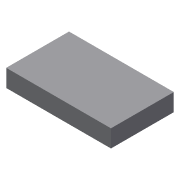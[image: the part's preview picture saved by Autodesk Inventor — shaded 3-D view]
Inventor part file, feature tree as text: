
AUTODESK INVENTOR PART (.ipt)
format: ipt  version: 2019 (Build 230136000, 136)  size: 72,192 bytes
history: native  units: mm
features: other x1, extrude x1, sketch x1
ambient origin geometry x8: Origin, YZ Plane, XZ Plane, XY Plane, X Axis, Y Axis, Z Axis, Center Point
bodies: Body1 (feature_tree)
feature tree (3):
  other  "솔리드1"
  extrude  "돌출1"  Depth=300.0mm
  sketch  "스케치1"
